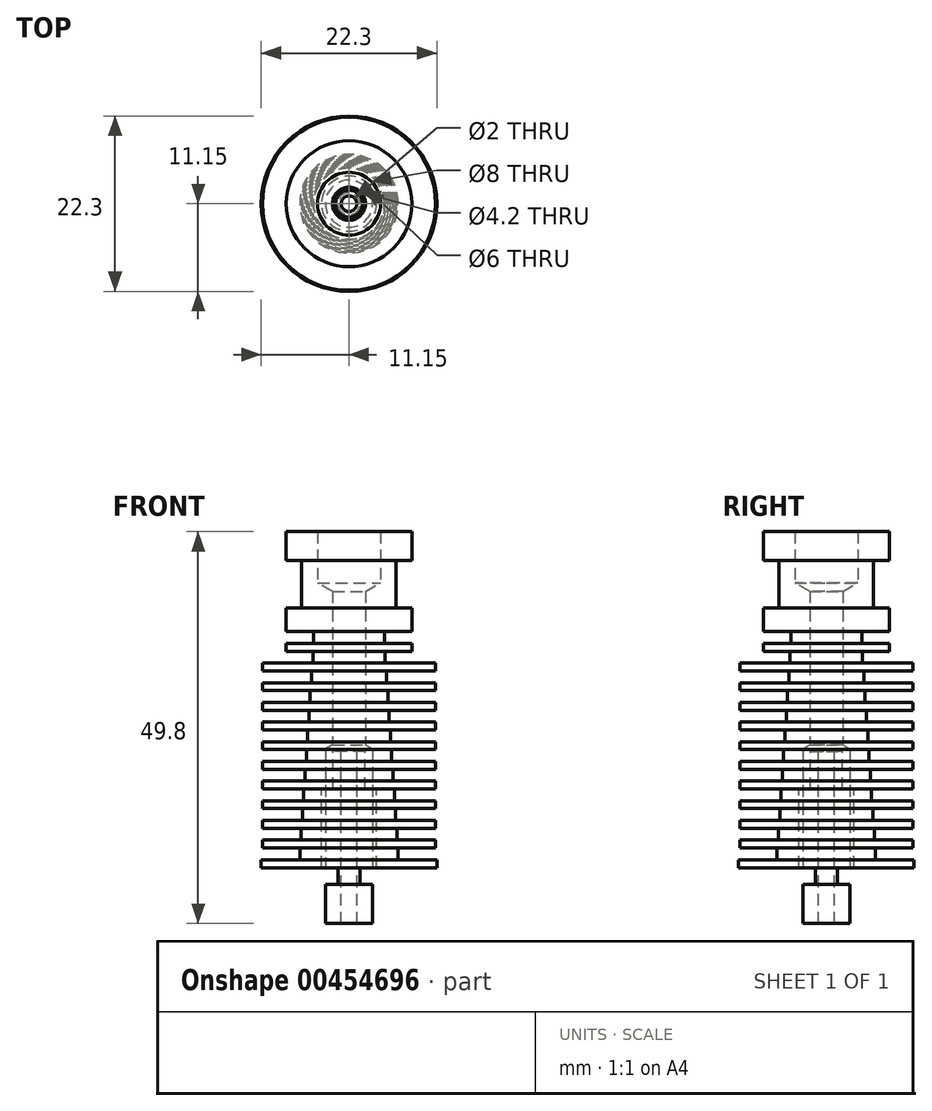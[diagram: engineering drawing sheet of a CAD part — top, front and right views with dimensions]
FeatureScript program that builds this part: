
annotation { "Feature Type Name" : "Feature", "Feature Type Description" : "" }
export const myFeature = defineFeature(function(context is Context, id is Id, definition is map)
    precondition{}
    {
        {
            var Q0;
            Q0=qCreatedBy(makeId("Front.planeOp"),FACE);
            var sketch = newSketch(context, id + "F0", { "sketchPlane" : qUnion([Q0])});
            skLineSegment(sketch, "E0", {"start": v(0, 0) * mm, "end": v(0, 42.7) * mm, "construction": true});
            skLineSegment(sketch, "E1", {"start": v(0, 0) * mm, "end": v(-11.15, 0) * mm});
            skLineSegment(sketch, "E2", {"start": v(-11.15, 0) * mm, "end": v(-11.15, 1) * mm});
            skLineSegment(sketch, "E3", {"start": v(-11.15, 1) * mm, "end": v(0, 1) * mm});
            skLineSegment(sketch, "E4", {"start": v(0, 1) * mm, "end": v(0, 0) * mm});
            skLineSegment(sketch, "E5.bottom", {"start": v(0, 2.5) * mm, "end": v(-11, 2.5) * mm});
            skLineSegment(sketch, "E5.top", {"start": v(0, 3.5) * mm, "end": v(-11, 3.5) * mm});
            skLineSegment(sketch, "E5.left", {"start": v(0, 2.5) * mm, "end": v(0, 3.5) * mm});
            skLineSegment(sketch, "E5.right", {"start": v(-11, 2.5) * mm, "end": v(-11, 3.5) * mm});
            skLineSegment(sketch, "E6.0.1.0", {"start": v(-11, 5) * mm, "end": v(-11, 6) * mm});
            skLineSegment(sketch, "E6.0.1.1", {"start": v(0, 5) * mm, "end": v(-11, 5) * mm});
            skLineSegment(sketch, "E6.0.1.2", {"start": v(0, 6) * mm, "end": v(-11, 6) * mm});
            skLineSegment(sketch, "E6.0.1.3", {"start": v(0, 5) * mm, "end": v(0, 6) * mm});
            skLineSegment(sketch, "E6.0.2.0", {"start": v(-11, 7.5) * mm, "end": v(-11, 8.5) * mm});
            skLineSegment(sketch, "E6.0.2.1", {"start": v(0, 7.5) * mm, "end": v(-11, 7.5) * mm});
            skLineSegment(sketch, "E6.0.2.2", {"start": v(0, 8.5) * mm, "end": v(-11, 8.5) * mm});
            skLineSegment(sketch, "E6.0.2.3", {"start": v(0, 7.5) * mm, "end": v(0, 8.5) * mm});
            skLineSegment(sketch, "E6.0.3.0", {"start": v(-11, 10) * mm, "end": v(-11, 11) * mm});
            skLineSegment(sketch, "E6.0.3.1", {"start": v(0, 10) * mm, "end": v(-11, 10) * mm});
            skLineSegment(sketch, "E6.0.3.2", {"start": v(0, 11) * mm, "end": v(-11, 11) * mm});
            skLineSegment(sketch, "E6.0.3.3", {"start": v(0, 10) * mm, "end": v(0, 11) * mm});
            skLineSegment(sketch, "E6.0.4.0", {"start": v(-11, 12.5) * mm, "end": v(-11, 13.5) * mm});
            skLineSegment(sketch, "E6.0.4.1", {"start": v(0, 12.5) * mm, "end": v(-11, 12.5) * mm});
            skLineSegment(sketch, "E6.0.4.2", {"start": v(0, 13.5) * mm, "end": v(-11, 13.5) * mm});
            skLineSegment(sketch, "E6.0.4.3", {"start": v(0, 12.5) * mm, "end": v(0, 13.5) * mm});
            skLineSegment(sketch, "E6.0.5.0", {"start": v(-11, 15) * mm, "end": v(-11, 16) * mm});
            skLineSegment(sketch, "E6.0.5.1", {"start": v(0, 15) * mm, "end": v(-11, 15) * mm});
            skLineSegment(sketch, "E6.0.5.2", {"start": v(0, 16) * mm, "end": v(-11, 16) * mm});
            skLineSegment(sketch, "E6.0.5.3", {"start": v(0, 15) * mm, "end": v(0, 16) * mm});
            skLineSegment(sketch, "E6.0.6.0", {"start": v(-11, 17.5) * mm, "end": v(-11, 18.5) * mm});
            skLineSegment(sketch, "E6.0.6.1", {"start": v(0, 17.5) * mm, "end": v(-11, 17.5) * mm});
            skLineSegment(sketch, "E6.0.6.2", {"start": v(0, 18.5) * mm, "end": v(-11, 18.5) * mm});
            skLineSegment(sketch, "E6.0.6.3", {"start": v(0, 17.5) * mm, "end": v(0, 18.5) * mm});
            skLineSegment(sketch, "E6.0.7.0", {"start": v(-11, 20) * mm, "end": v(-11, 21) * mm});
            skLineSegment(sketch, "E6.0.7.1", {"start": v(0, 20) * mm, "end": v(-11, 20) * mm});
            skLineSegment(sketch, "E6.0.7.2", {"start": v(0, 21) * mm, "end": v(-11, 21) * mm});
            skLineSegment(sketch, "E6.0.7.3", {"start": v(0, 20) * mm, "end": v(0, 21) * mm});
            skLineSegment(sketch, "E6.0.8.0", {"start": v(-11, 22.5) * mm, "end": v(-11, 23.5) * mm});
            skLineSegment(sketch, "E6.0.8.1", {"start": v(0, 22.5) * mm, "end": v(-11, 22.5) * mm});
            skLineSegment(sketch, "E6.0.8.2", {"start": v(0, 23.5) * mm, "end": v(-11, 23.5) * mm});
            skLineSegment(sketch, "E6.0.8.3", {"start": v(0, 22.5) * mm, "end": v(0, 23.5) * mm});
            skLineSegment(sketch, "E6.0.9.0", {"start": v(-11, 25) * mm, "end": v(-11, 26) * mm});
            skLineSegment(sketch, "E6.0.9.1", {"start": v(0, 25) * mm, "end": v(-11, 25) * mm});
            skLineSegment(sketch, "E6.0.9.2", {"start": v(0, 26) * mm, "end": v(-11, 26) * mm});
            skLineSegment(sketch, "E6.0.9.3", {"start": v(0, 25) * mm, "end": v(0, 26) * mm});
            skLineSegment(sketch, "E6.direction1", {"start": v(-11, 2.5) * mm, "end": v(14, 2.5) * mm, "construction": true});
            skLineSegment(sketch, "E6.direction2", {"start": v(-11, 2.5) * mm, "end": v(-11, 5) * mm, "construction": true});
            skLineSegment(sketch, "E7", {"start": v(0, 42.7) * mm, "end": v(-8, 42.7) * mm});
            skLineSegment(sketch, "E8", {"start": v(-8, 42.7) * mm, "end": v(-8, 39) * mm});
            skLineSegment(sketch, "E9", {"start": v(-8, 39) * mm, "end": v(-6, 39) * mm});
            skLineSegment(sketch, "E10", {"start": v(-6, 39) * mm, "end": v(-6, 33) * mm});
            skLineSegment(sketch, "E11", {"start": v(-6, 33) * mm, "end": v(-8, 33) * mm});
            skLineSegment(sketch, "E12", {"start": v(-8, 33) * mm, "end": v(-8, 30) * mm});
            skLineSegment(sketch, "E13", {"start": v(-8, 30) * mm, "end": v(0, 30) * mm});
            skLineSegment(sketch, "E14.bottom", {"start": v(-8, 28.5) * mm, "end": v(0, 28.5) * mm});
            skLineSegment(sketch, "E14.top", {"start": v(-8, 27.5) * mm, "end": v(0, 27.5) * mm});
            skLineSegment(sketch, "E14.left", {"start": v(-8, 28.5) * mm, "end": v(-8, 27.5) * mm});
            skLineSegment(sketch, "E14.right", {"start": v(0, 28.5) * mm, "end": v(0, 27.5) * mm});
            skLineSegment(sketch, "E15", {"start": v(0, 42.7) * mm, "end": v(0, 30) * mm});
            skLineSegment(sketch, "E16.left", {"start": v(0, 42.7) * mm, "end": v(0, 0) * mm});
            skPoint(sketch, "E17", {"position": v(-4, 42.7) * mm});
            skLineSegment(sketch, "E18", {"start": v(-4.5, 27.5) * mm, "end": v(-6.25, 1) * mm, "construction": true});
            skLineSegment(sketch, "E19", {"start": v(-4.5, 27.5) * mm, "end": v(-4.5, 30) * mm});
            skLineSegment(sketch, "E20", {"start": v(-6.25, 1) * mm, "end": v(-6.25, 2.5) * mm});
            skLineSegment(sketch, "E21", {"start": v(-6.08, 3.5) * mm, "end": v(-6.08, 5) * mm});
            skLineSegment(sketch, "E22", {"start": v(-5.92, 6) * mm, "end": v(-5.92, 7.5) * mm});
            skLineSegment(sketch, "E23", {"start": v(-5.75, 8.5) * mm, "end": v(-5.75, 10) * mm});
            skLineSegment(sketch, "E24", {"start": v(-5.59, 11) * mm, "end": v(-5.59, 12.5) * mm});
            skLineSegment(sketch, "E25", {"start": v(-5.42, 13.5) * mm, "end": v(-5.42, 15) * mm});
            skLineSegment(sketch, "E26", {"start": v(-5.26, 16) * mm, "end": v(-5.26, 17.5) * mm});
            skLineSegment(sketch, "E27", {"start": v(-5.1, 18.5) * mm, "end": v(-5.1, 20) * mm});
            skLineSegment(sketch, "E28", {"start": v(-4.93, 21) * mm, "end": v(-4.93, 22.5) * mm});
            skLineSegment(sketch, "E29", {"start": v(-4.76, 23.5) * mm, "end": v(-4.76, 25) * mm});
            skLineSegment(sketch, "E30", {"start": v(-4.6, 26) * mm, "end": v(-4.6, 27.5) * mm});
            skSolve(sketch);
        }
        {
            var Q0;
            Q0=qSketchRegion(id+"F0",true);
            var Q1;
            Q1=sQuery(id+"F0.wireOp",EDGE,"E0");
            revolve(context, id + "F1", {"entities" : qUnion([Q0]), "axis" : qUnion([Q1]), "revolveType" : RevolveType.FULL});
        }
        {
            var Q0;
            Q0=qCreatedBy(makeId("Front.planeOp"),FACE);
            var sketch = newSketch(context, id + "F2", { "sketchPlane" : qUnion([Q0])});
            skLineSegment(sketch, "E31", {"start": v(-2.1, 0) * mm, "end": v(-3, 0) * mm});
            skLineSegment(sketch, "E32", {"start": v(-3, 0) * mm, "end": v(-3, 15.1) * mm});
            skLineSegment(sketch, "E33", {"start": v(-3, 15.1) * mm, "end": v(-2.1, 15.62) * mm});
            skLineSegment(sketch, "E34", {"start": v(-2.1, 15.62) * mm, "end": v(-2.1, 35.1) * mm});
            skLineSegment(sketch, "E35", {"start": v(-2.1, 35.1) * mm, "end": v(-4, 36.2) * mm});
            skLineSegment(sketch, "E36", {"start": v(-4, 36.2) * mm, "end": v(-4, 42.7) * mm});
            skLineSegment(sketch, "E37", {"start": v(-4, 42.7) * mm, "end": v(-2.1, 42.7) * mm});
            skLineSegment(sketch, "E38", {"start": v(0, 0) * mm, "end": v(0, 42.7) * mm, "construction": true});
            skLineSegment(sketch, "E39", {"start": v(-2.1, 42.7) * mm, "end": v(0, 42.7) * mm});
            skLineSegment(sketch, "E40", {"start": v(0, 0) * mm, "end": v(-2.1, 0) * mm});
            skLineSegment(sketch, "E41", {"start": v(0, 42.7) * mm, "end": v(0, 0) * mm});
            skSolve(sketch);
        }
        {
            var Q0;
            Q0=qSketchRegion(id+"F2",true);
            var Q1;
            Q1=sQuery(id+"F2.wireOp",EDGE,"E38");
            revolve(context, id + "F3", {"entities" : qUnion([Q0]), "axis" : qUnion([Q1]), "revolveType" : RevolveType.FULL});
        }
        {
            var Q0;
            Q0=makeQuery(id+"F3.opRevolve","SWEPT_BODY",BODY,{"disambiguationData":[OSD([sQuery(id+"F2.wireOp",EDGE,"E31"),sQuery(id+"F2.wireOp",EDGE,"E32"),sQuery(id+"F2.wireOp",EDGE,"E33"),sQuery(id+"F2.wireOp",EDGE,"E34"),sQuery(id+"F2.wireOp",EDGE,"E35"),sQuery(id+"F2.wireOp",EDGE,"E36"),sQuery(id+"F2.wireOp",EDGE,"E37"),sQuery(id+"F2.wireOp",EDGE,"E39"),sQuery(id+"F2.wireOp",EDGE,"E40"),sQuery(id+"F2.wireOp",EDGE,"E41")])]});
            var Q1;
            Q1=makeQuery(id+"F1.opRevolve","SWEPT_BODY",BODY,{"disambiguationData":[OSD([sQuery(id+"F0.wireOp",EDGE,"E1"),sQuery(id+"F0.wireOp",EDGE,"E2"),sQuery(id+"F0.wireOp",EDGE,"E3"),sQuery(id+"F0.wireOp",EDGE,"E5.bottom"),sQuery(id+"F0.wireOp",EDGE,"E5.top"),sQuery(id+"F0.wireOp",EDGE,"E5.right"),sQuery(id+"F0.wireOp",EDGE,"E6.0.1.0"),sQuery(id+"F0.wireOp",EDGE,"E6.0.1.1"),sQuery(id+"F0.wireOp",EDGE,"E6.0.1.2"),sQuery(id+"F0.wireOp",EDGE,"E6.0.2.0"),sQuery(id+"F0.wireOp",EDGE,"E6.0.2.1"),sQuery(id+"F0.wireOp",EDGE,"E6.0.2.2"),sQuery(id+"F0.wireOp",EDGE,"E6.0.3.0"),sQuery(id+"F0.wireOp",EDGE,"E6.0.3.1"),sQuery(id+"F0.wireOp",EDGE,"E6.0.3.2"),sQuery(id+"F0.wireOp",EDGE,"E6.0.4.0"),sQuery(id+"F0.wireOp",EDGE,"E6.0.4.1"),sQuery(id+"F0.wireOp",EDGE,"E6.0.4.2"),sQuery(id+"F0.wireOp",EDGE,"E6.0.5.0"),sQuery(id+"F0.wireOp",EDGE,"E6.0.5.1"),sQuery(id+"F0.wireOp",EDGE,"E6.0.5.2"),sQuery(id+"F0.wireOp",EDGE,"E6.0.6.0"),sQuery(id+"F0.wireOp",EDGE,"E6.0.6.1"),sQuery(id+"F0.wireOp",EDGE,"E6.0.6.2"),sQuery(id+"F0.wireOp",EDGE,"E6.0.7.0"),sQuery(id+"F0.wireOp",EDGE,"E6.0.7.1"),sQuery(id+"F0.wireOp",EDGE,"E6.0.7.2"),sQuery(id+"F0.wireOp",EDGE,"E6.0.8.0"),sQuery(id+"F0.wireOp",EDGE,"E6.0.8.1"),sQuery(id+"F0.wireOp",EDGE,"E6.0.8.2"),sQuery(id+"F0.wireOp",EDGE,"E6.0.9.0"),sQuery(id+"F0.wireOp",EDGE,"E6.0.9.1"),sQuery(id+"F0.wireOp",EDGE,"E6.0.9.2"),sQuery(id+"F0.wireOp",EDGE,"E7"),sQuery(id+"F0.wireOp",EDGE,"E8"),sQuery(id+"F0.wireOp",EDGE,"E9"),sQuery(id+"F0.wireOp",EDGE,"E10"),sQuery(id+"F0.wireOp",EDGE,"E11"),sQuery(id+"F0.wireOp",EDGE,"E12"),sQuery(id+"F0.wireOp",EDGE,"E13"),sQuery(id+"F0.wireOp",EDGE,"E14.bottom"),sQuery(id+"F0.wireOp",EDGE,"E14.top"),sQuery(id+"F0.wireOp",EDGE,"E14.left"),sQuery(id+"F0.wireOp",EDGE,"E16.bottom"),sQuery(id+"F0.wireOp",EDGE,"E16.top"),sQuery(id+"F0.wireOp",EDGE,"E16.left"),sQuery(id+"F0.wireOp",EDGE,"E16.right")])]});
            booleanBodies(context, id + "F4", {"operationType" : BooleanOperationType.SUBTRACTION, "tools" : qUnion([Q0]), "targets" : qUnion([Q1])});
        }
        {
            var Q0;
            Q0=qCreatedBy(makeId("Front.planeOp"),FACE);
            var sketch = newSketch(context, id + "F5", { "sketchPlane" : qUnion([Q0])});
            skLineSegment(sketch, "E42", {"start": v(0, 0) * mm, "end": v(0, 15.1) * mm, "construction": true});
            skLineSegment(sketch, "E43", {"start": v(0, 0) * mm, "end": v(0, -7.1) * mm, "construction": true});
            skLineSegment(sketch, "E44", {"start": v(-1.4, 0) * mm, "end": v(-1.4, -2.1) * mm});
            skLineSegment(sketch, "E45", {"start": v(-1.4, -2.1) * mm, "end": v(-3, -2.1) * mm});
            skLineSegment(sketch, "E46", {"start": v(-3, -2.1) * mm, "end": v(-3, -7.1) * mm});
            skLineSegment(sketch, "E47", {"start": v(-3, -7.1) * mm, "end": v(-1, -7.1) * mm});
            skLineSegment(sketch, "E48", {"start": v(-1, -7.1) * mm, "end": v(-1, 15.1) * mm});
            skLineSegment(sketch, "E49", {"start": v(-1, 15.1) * mm, "end": v(-1.71, 15.1) * mm});
            skLineSegment(sketch, "E50", {"start": v(-2.02, 14.8) * mm, "end": v(-2.02, 9.97) * mm});
            skLineSegment(sketch, "E51", {"start": v(-2.02, 9.97) * mm, "end": v(-3.5, 9.97) * mm});
            skLineSegment(sketch, "E52", {"start": v(-3.5, 9.97) * mm, "end": v(-3.5, 0) * mm});
            skLineSegment(sketch, "E53", {"start": v(-3.5, 0) * mm, "end": v(-1.4, 0) * mm});
            skLineSegment(sketch, "E54", {"start": v(-2.02, 14.8) * mm, "end": v(-1.71, 15.1) * mm});
            skSolve(sketch);
        }
        {
            var Q0;
            Q0=qSketchRegion(id+"F5",true);
            var Q1;
            Q1=sQuery(id+"F5.wireOp",EDGE,"E43");
            revolve(context, id + "F6", {"entities" : qUnion([Q0]), "axis" : qUnion([Q1]), "revolveType" : RevolveType.FULL});
        }
    });
